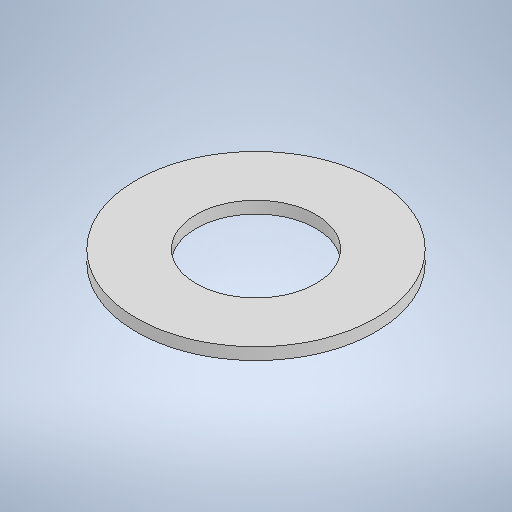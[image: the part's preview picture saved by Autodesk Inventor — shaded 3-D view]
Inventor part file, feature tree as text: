
AUTODESK INVENTOR PART (.ipt)
format: ipt  version: 2025.1 (Build 291241000, 241)  size: 237,056 bytes
history: native  units: mm
features: extrude x1, sketch x1
ambient origin geometry x8: Origin, YZ Plane, XZ Plane, XY Plane, X Axis, Y Axis, Z Axis, Center Point
bodies: Solid1 (feature_tree)
feature tree (2):
  extrude  "Extrusion1"  Depth=5.0mm
  sketch  "Sketch1"  dims[d0=10.0mm d1=5.0mm d2=0.5mm d3=0.0mm]
